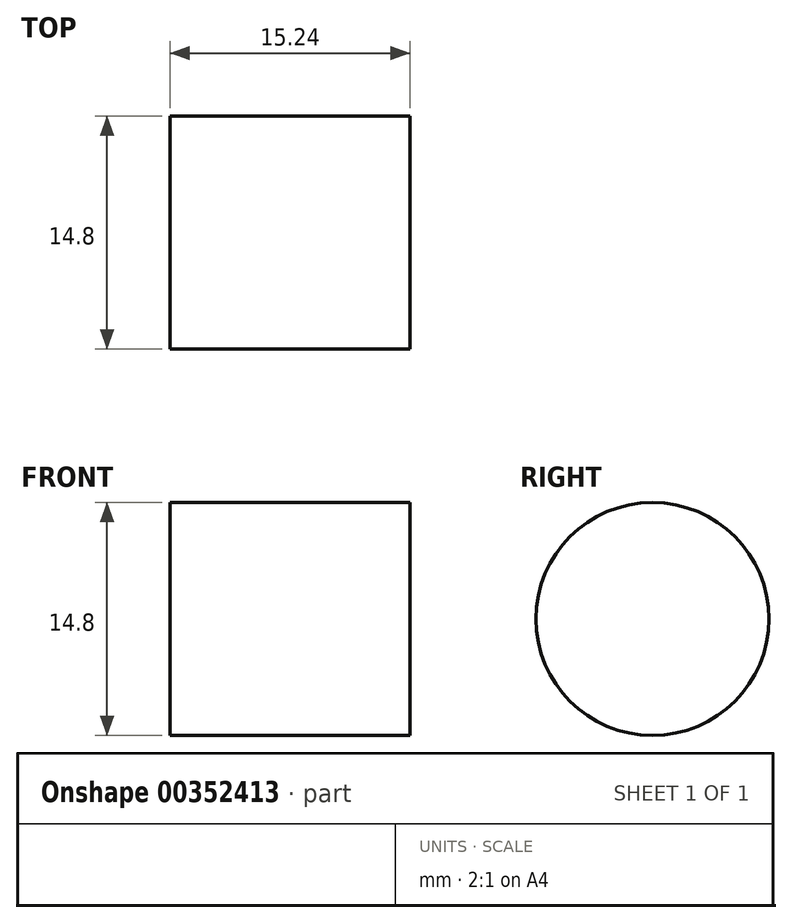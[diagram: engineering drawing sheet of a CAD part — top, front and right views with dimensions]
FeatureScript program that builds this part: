
annotation { "Feature Type Name" : "Feature", "Feature Type Description" : "" }
export const myFeature = defineFeature(function(context is Context, id is Id, definition is map)
    precondition{}
    {
        {
            var Q0;
            Q0=qCreatedBy(makeId("Right.planeOp"),FACE);
            var sketch = newSketch(context, id + "F0", { "sketchPlane" : qUnion([Q0])});
            skCircle(sketch, "E0", {"center": v(0, 0) * mm, "radius": 7.4 * mm});
            skSolve(sketch);
        }
        {
            var Q0;
            Q0=makeQuery(id+"F0.imprint","IMPRINT",FACE,{"disambiguationData":[TD([[makeQuery(id+"F0.imprint","IMPRINT",EDGE,{"derivedFrom":sQuery(id+"F0.wireOp",EDGE,"E0")}),1.0]])]});
            extrude(context, id + "F1", {"entities" : qUnion([Q0]), "depth" : 15.24 * mm});
        }
    });
